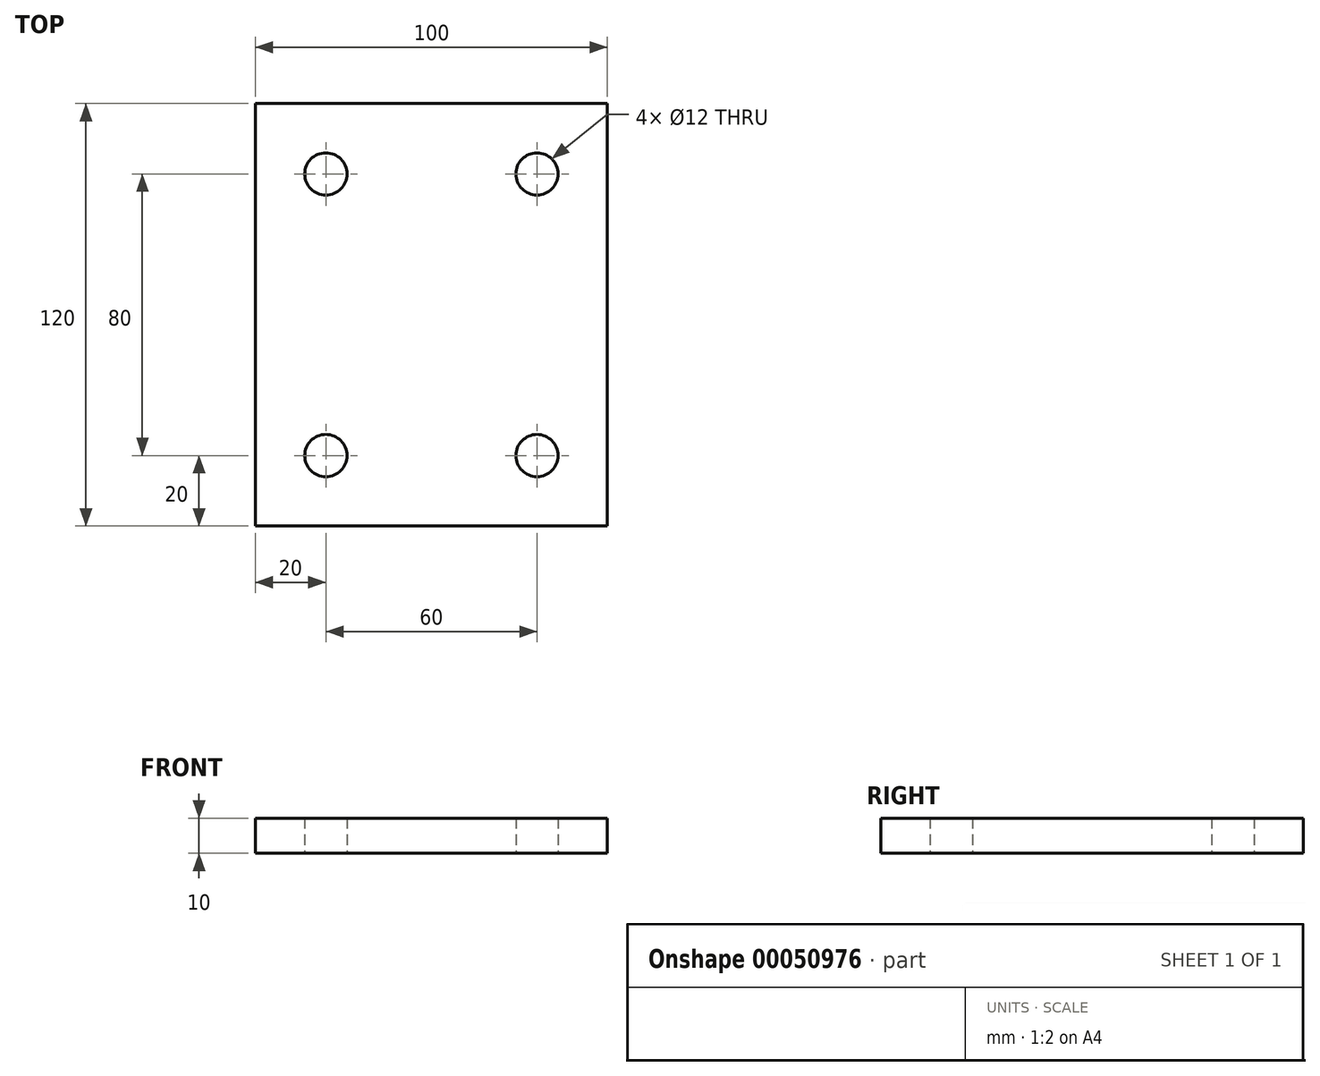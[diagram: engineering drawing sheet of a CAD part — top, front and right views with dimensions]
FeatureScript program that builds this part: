
annotation { "Feature Type Name" : "Feature", "Feature Type Description" : "" }
export const myFeature = defineFeature(function(context is Context, id is Id, definition is map)
    precondition{}
    {
        {
            var Q0;
            Q0=qCreatedBy(makeId("Top.planeOp"),FACE);
            var sketch = newSketch(context, id + "F0", { "sketchPlane" : qUnion([Q0])});
            skLineSegment(sketch, "E0.rect.bottom", {"start": v(-50, -60) * mm, "end": v(50, -60) * mm});
            skLineSegment(sketch, "E0.rect.top", {"start": v(-50, 60) * mm, "end": v(50, 60) * mm});
            skLineSegment(sketch, "E0.rect.left", {"start": v(-50, -60) * mm, "end": v(-50, 60) * mm});
            skLineSegment(sketch, "E0.rect.right", {"start": v(50, -60) * mm, "end": v(50, 60) * mm});
            skPoint(sketch, "E0.rect.middle", {"position": v(0, 0) * mm});
            skCircle(sketch, "E1", {"center": v(-30, 40) * mm, "radius": 6 * mm});
            skCircle(sketch, "E2.MirrorC", {"center": v(30, 40) * mm, "radius": 6 * mm});
            skCircle(sketch, "E3.MirrorC", {"center": v(-30, -40) * mm, "radius": 6 * mm});
            skCircle(sketch, "E4.MirrorC", {"center": v(30, -40) * mm, "radius": 6 * mm});
            skSolve(sketch);
        }
        {
            var Q0;
            Q0=makeQuery(id+"F0.imprint","IMPRINT",FACE,{"disambiguationData":[TD([[makeQuery(id+"F0.imprint","IMPRINT",EDGE,{"derivedFrom":sQuery(id+"F0.wireOp",EDGE,"E0.rect.bottom")}),1.0]])]});
            extrude(context, id + "F1", {"entities" : qUnion([Q0]), "depth" : 10 * mm});
        }
    });
